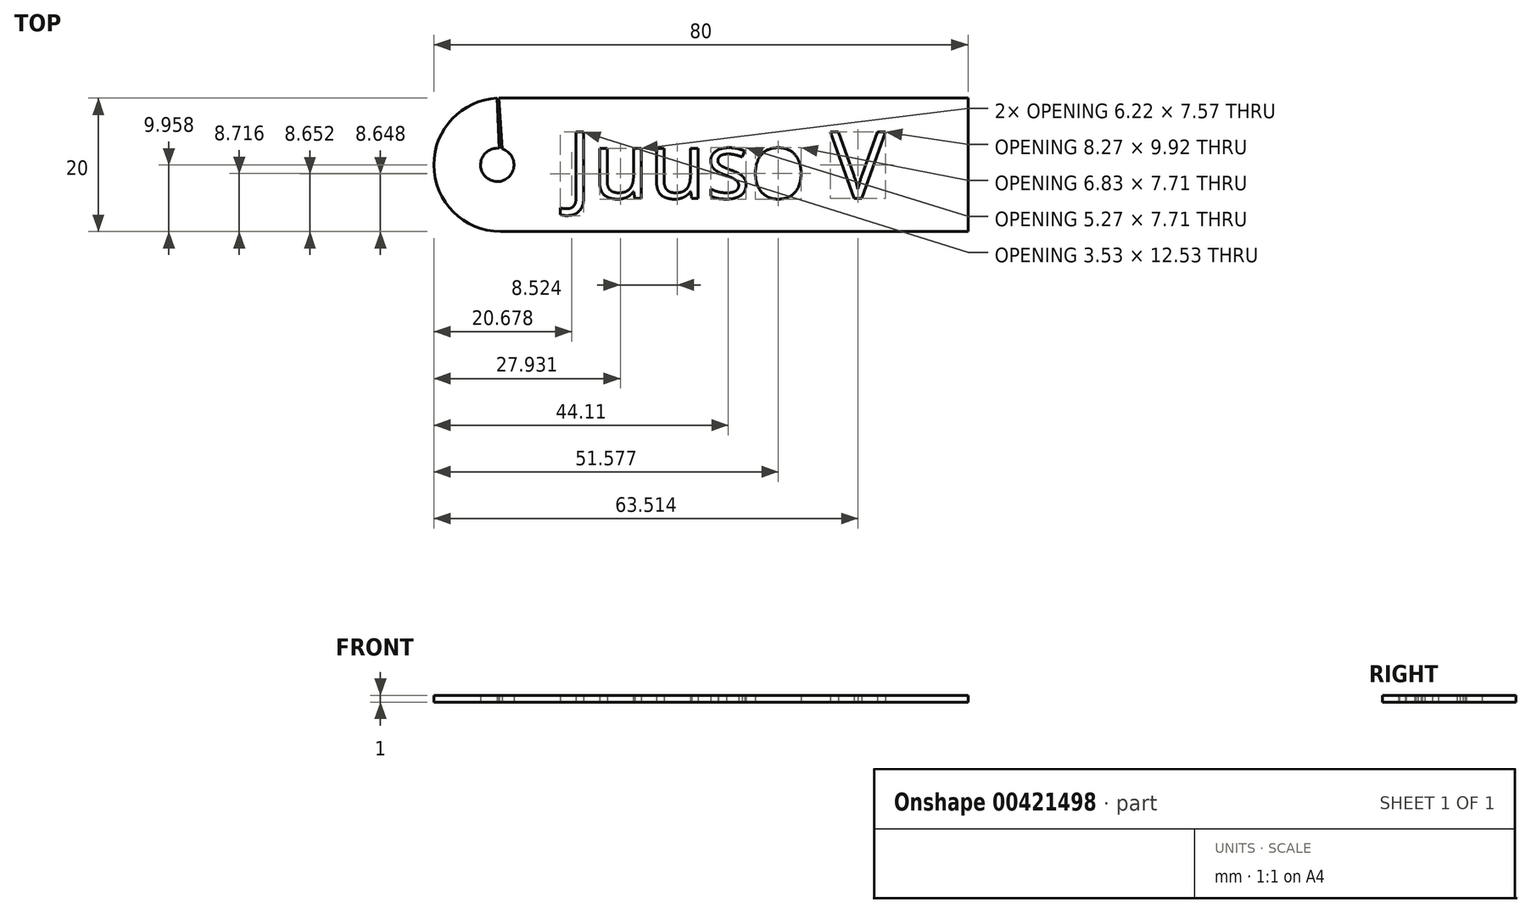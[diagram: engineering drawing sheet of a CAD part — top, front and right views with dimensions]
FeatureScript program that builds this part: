
annotation { "Feature Type Name" : "Feature", "Feature Type Description" : "" }
export const myFeature = defineFeature(function(context is Context, id is Id, definition is map)
    precondition{}
    {
        {
            var Q0;
            Q0=qCreatedBy(makeId("Top.planeOp"),FACE);
            var sketch = newSketch(context, id + "F0", { "sketchPlane" : qUnion([Q0])});
            skLineSegment(sketch, "E0.bottom", {"start": v(40, -10) * mm, "end": v(-40, -10) * mm});
            skLineSegment(sketch, "E0.top", {"start": v(40, 10) * mm, "end": v(-40, 10) * mm});
            skLineSegment(sketch, "E0.left", {"start": v(40, -10) * mm, "end": v(40, 10) * mm});
            skLineSegment(sketch, "E0.right", {"start": v(-40, -10) * mm, "end": v(-40, 10) * mm});
            skPoint(sketch, "E0.middle", {"position": v(0, 0) * mm});
            skCircle(sketch, "E1", {"center": v(-30.5, 0) * mm, "radius": 2.5 * mm});
            skPoint(sketch, "E2.centerSnap0", {"position": v(-40, 0) * mm});
            skLineSegment(sketch, "E3.0", {"start": v(-30, 13.9) * mm, "end": v(-30, 33.9) * mm});
            skText(sketch, "E4", { "text": "Juuso V", "fontName": "OpenSans-Regular.ttf"});
            skLineSegment(sketch, "E5", {"start": v(-30.3, 10) * mm, "end": v(-30.5, 10) * mm});
            skLineSegment(sketch, "E6", {"start": v(-30.5, 0) * mm, "end": v(-30, 0.05) * mm});
            skLineSegment(sketch, "E7", {"start": v(-30.5, 10) * mm, "end": v(-30.21, 2.48) * mm});
            skLineSegment(sketch, "E8", {"start": v(-30.3, 10) * mm, "end": v(-29.77, 2.4) * mm});
            const initialGuessF0  = {"E4": [-0.02, -0.005, 1, 0, 0.01]};
            skSetInitialGuess(sketch, initialGuessF0);
            skSolve(sketch);
        }
        {
            var Q0;
            Q0=makeQuery(id+"F0.imprint","IMPRINT",FACE,{"disambiguationData":[TD([[makeQuery(id+"F0.imprint","IMPRINT",EDGE,{"derivedFrom":sQuery(id+"F0.wireOp",EDGE,"E0.bottom")}),-1.0]])]});
            extrude(context, id + "F1", {"entities" : qUnion([Q0]), "depth" : 1 * mm});
        }
        {
            var Q0;
            Q0=makeQuery(id+"F1.opExtrude","SWEPT_EDGE",EDGE,{"disambiguationData":[OSD([sQuery(id+"F0.wireOp",EDGE,"E0.top"),sQuery(id+"F0.wireOp",EDGE,"E0.right")])]});
            var Q1;
            Q1=makeQuery(id+"F1.opExtrude","SWEPT_EDGE",EDGE,{"disambiguationData":[OSD([sQuery(id+"F0.wireOp",EDGE,"E0.bottom"),sQuery(id+"F0.wireOp",EDGE,"E0.right")])]});
            fillet(context, id + "F2", {"entities" : qUnion([Q0, Q1]), "radius" : 10 * mm, "tangentPropagation" : true, "allowEdgeOverflow" : false});
        }
    });
